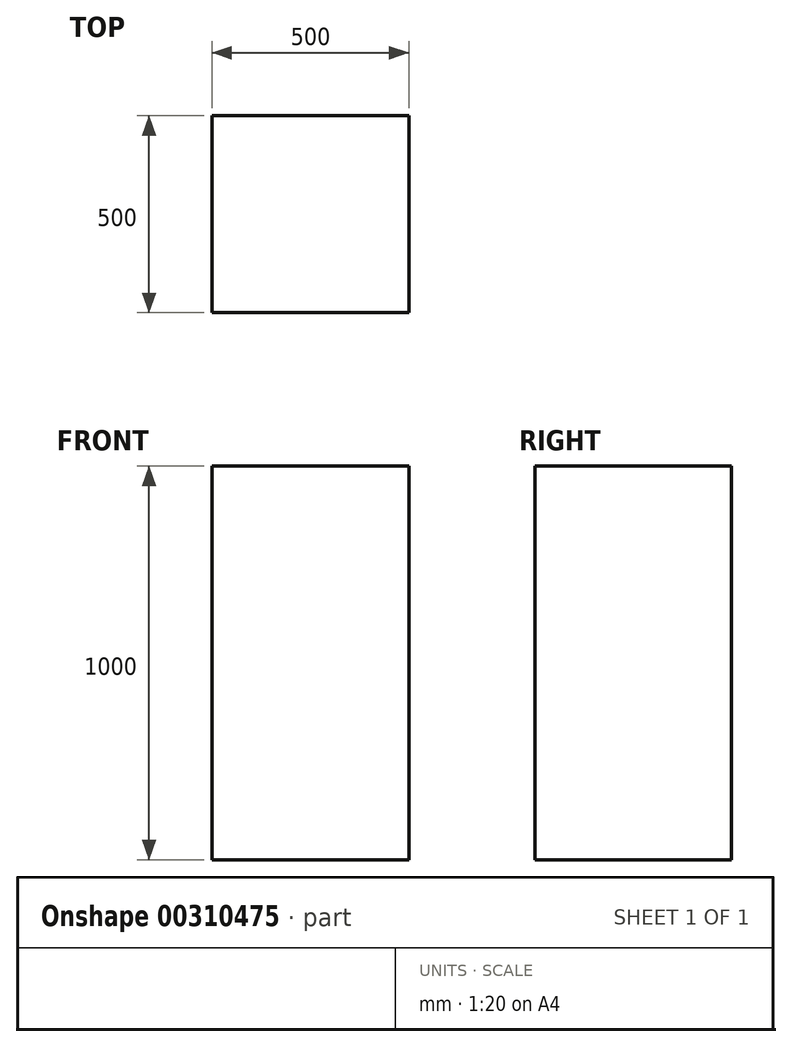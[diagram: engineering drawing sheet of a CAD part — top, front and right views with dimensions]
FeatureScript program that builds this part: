
annotation { "Feature Type Name" : "Feature", "Feature Type Description" : "" }
export const myFeature = defineFeature(function(context is Context, id is Id, definition is map)
    precondition{}
    {
        {
            var Q0;
            Q0=qCreatedBy(makeId("Top.planeOp"),FACE);
            var sketch = newSketch(context, id + "F0", { "sketchPlane" : qUnion([Q0])});
            skLineSegment(sketch, "E0.bottom", {"start": v(250, 250) * mm, "end": v(-250, 250) * mm});
            skLineSegment(sketch, "E0.top", {"start": v(250, -250) * mm, "end": v(-250, -250) * mm});
            skLineSegment(sketch, "E0.left", {"start": v(250, 250) * mm, "end": v(250, -250) * mm});
            skLineSegment(sketch, "E0.right", {"start": v(-250, 250) * mm, "end": v(-250, -250) * mm});
            skPoint(sketch, "E0.middle", {"position": v(0, 0) * mm});
            skSolve(sketch);
        }
        {
            var Q0;
            Q0=makeQuery(id+"F0.imprint","IMPRINT",FACE,{"disambiguationData":[TD([[makeQuery(id+"F0.imprint","IMPRINT",EDGE,{"derivedFrom":sQuery(id+"F0.wireOp",EDGE,"E0.bottom")}),1.0]])]});
            extrude(context, id + "F1", {"entities" : qUnion([Q0]), "depth" : 1000 * mm});
        }
    });
